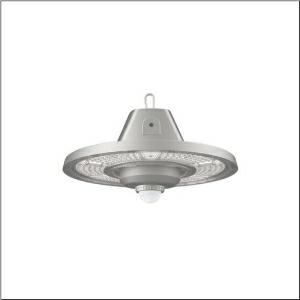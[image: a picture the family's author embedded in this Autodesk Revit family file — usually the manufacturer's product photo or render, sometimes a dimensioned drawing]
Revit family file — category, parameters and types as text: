
# Revit family: highbay_31-s_51hc427a4fmb01
name_source: partatom
category: Lighting Fixtures
units: mm (PartAtom-declared; Revit-internal decimal feet)

## family parameters
Cut with Voids When Loaded = No
Host = Face
Light Source = No
Part Type = Normal
Room Calculation Point = No
Round Connector Dimension = Use Diameter
Shared = No

## types (1)
- Highbay 31-S (1 x LED, 14000 lm, 94 W, 4000K)
    Apparent Load = 94 VA
    CIE Flux Codes = 77 99 100 100 100
    Color Rendering = 80
    Color Temperature = 4000K
    Default Elevation = 1800 mm
    Description = Highbay 31-S, LED high bay luminaire, primary light control with lens, of PC, primary optical cover: cover panel, of PC, transparent, light emission: direct distribution, primary light characteristic: rotationally symmetric, installation type: suspended mounting, surface-mounted, LED, rated luminous flux: 14.000lm, luminous efficacy: 150lm/W, light colour: 840, colour temperature: 4000K, control gear: ECG, with cable, 3x 1.0mm², free wire ends, mains connection: 220..240V, AC/DC, 0/50..60Hz, cable length: 1,5m, rated input power: 94W, housing, rotationally symmetric, of diecast aluminium, grey aluminium (RAL 9007), diameter: 339mm, PIR sensor, protection rating (complete): IP65, insulation class (complete): insulation class I (protective earthing), certification: CE, ENEC, UKCA, protection symbol: D, impact resistance: IK08, permissible operating ambient temperature: -30..+45°C, standard: EN 60598-2-22, EN 60598, corresponds to IFS (International Featured Standards) requirements for safety and quality in the food industry, packaging unit: 1 piece
    Height = 141 mm
    Lamp = 1 x LED
    Lamp Light Flux = 14000 lm
    Lamp Power = 94 W
    Lamp count = 1
    Length = 339 mm
    Luminous efficacy = 149 lm/W
    Manufacturer = Siteco
    ModVariant = No
    Model = 51HC427A4FMB01
    Mounting Place = Ceiling
    Mounting Type = Pendant
    Number of Poles = 1
    OnlyDefault = Yes
    Power Factor = 1
    Product Name = Highbay 31-S
    Product group = LED high bay luminaire
    ProductGroupID = 903
    Protection Class = Protection class I
    Protection Degree = IP 65
    RLX_Detail_Level = 1
    RlxData = <blob elided: 108461 chars, md5=e272e82e>
    Socket = socket
    Standby Power = 0 W
    System Light Flux = 14000 lm
    System Power = 94 W
    Type Comments = Product without accessories
    Type Image = l_384983.jpg
    URL = http://relux.com
    VarID = ---
    Voltage = 0 V
    Weight = 0.00 kg
    Width = 0 mm  [stored 0 ft]

note: [stored X ft] marks values corroborated as IEEE doubles in the binary element streams (Revit-internal decimal feet)

## geometry (parser evidence)
native form markers: Blend x4, Sweep x10
no freeform markers — native parametric forms only
